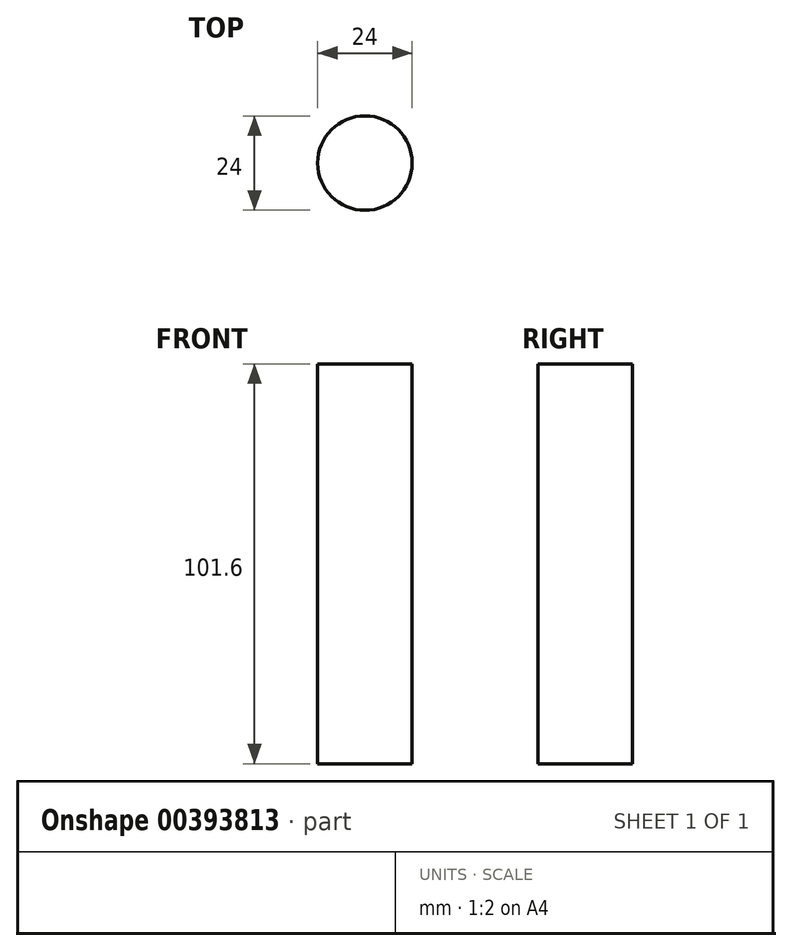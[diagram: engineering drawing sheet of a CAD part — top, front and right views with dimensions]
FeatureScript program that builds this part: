
annotation { "Feature Type Name" : "Feature", "Feature Type Description" : "" }
export const myFeature = defineFeature(function(context is Context, id is Id, definition is map)
    precondition{}
    {
        {
            var Q0;
            Q0=qCreatedBy(makeId("Top.planeOp"),FACE);
            var sketch = newSketch(context, id + "F0", { "sketchPlane" : qUnion([Q0])});
            skCircle(sketch, "E0", {"center": v(1.65, 0) * mm, "radius": 12 * mm});
            skSolve(sketch);
        }
        {
            var Q0;
            Q0=makeQuery(id+"F0.imprint","IMPRINT",FACE,{"disambiguationData":[TD([[makeQuery(id+"F0.imprint","IMPRINT",EDGE,{"derivedFrom":sQuery(id+"F0.wireOp",EDGE,"E0")}),1.0]])]});
            extrude(context, id + "F1", {"entities" : qUnion([Q0]), "depth" : 101.6 * mm});
        }
    });
